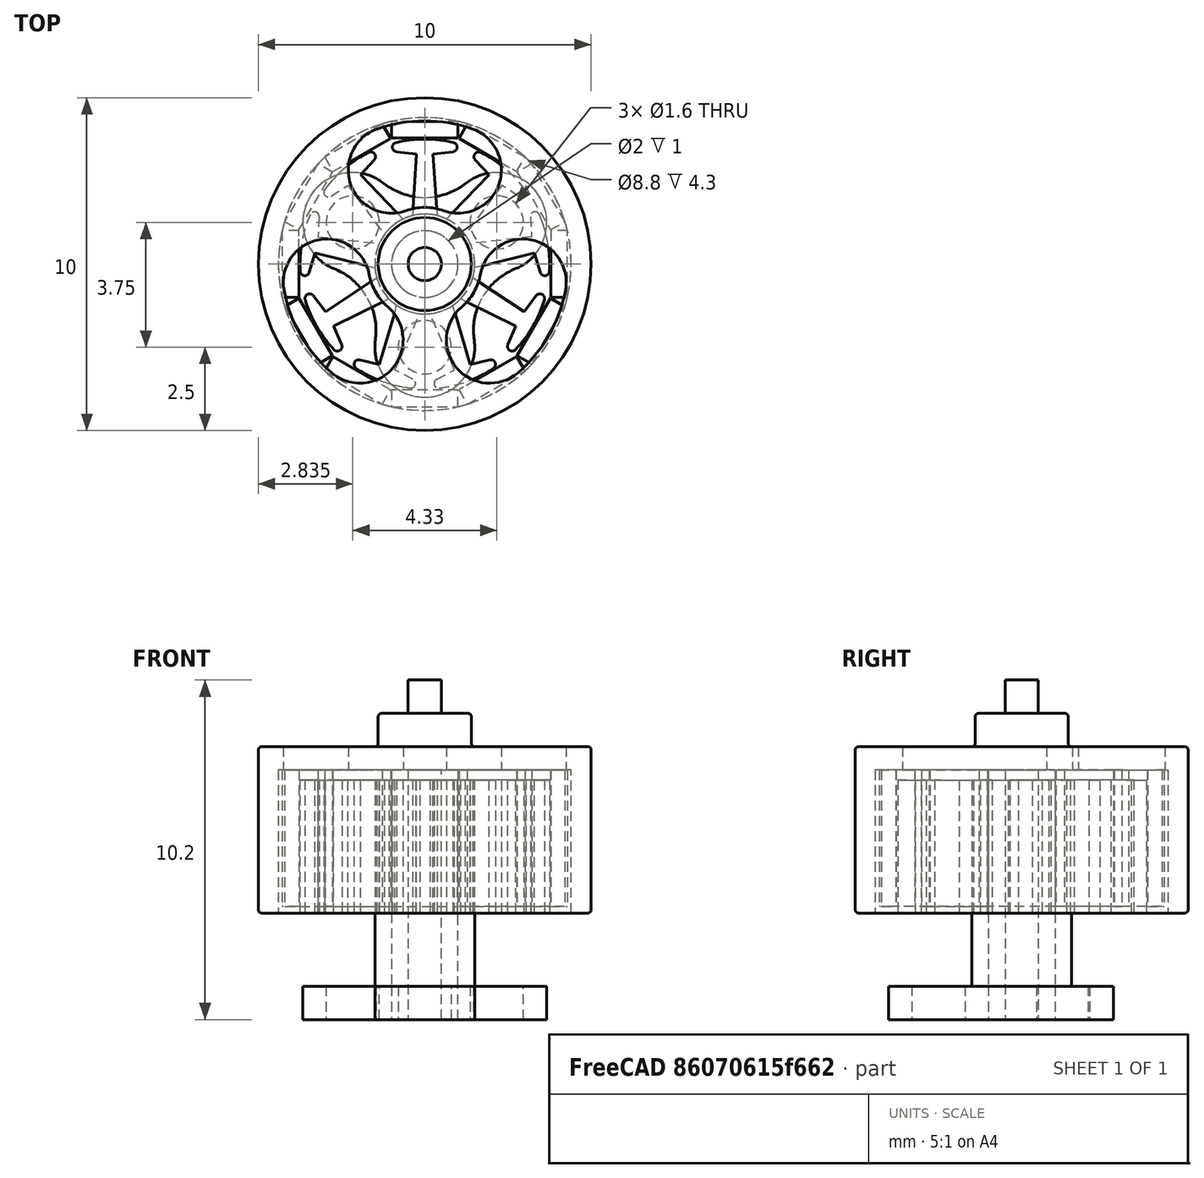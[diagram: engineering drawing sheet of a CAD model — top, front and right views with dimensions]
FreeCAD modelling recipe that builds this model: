
FCSTD DOCUMENT  (FreeCAD 0.18.1R)
Label: Moteur_D0703
License: All rights reserved
LicenseURL: http://en.wikipedia.org/wiki/All_rights_reserved
objects: Sketcher::SketchObject×9, PartDesign::Pad×7, PartDesign::PolarPattern×3, PartDesign::Pocket×2, PartDesign::Body×2, PartDesign::Fillet×1
note: 33 computed .brp shape members not serialized (recipe doc carries the construction recipe); baked Part::Feature solids carry a one-line shape summary decoded from their .brp

FEATURE [Sketcher::SketchObject] Sketch
  MapMode = 5
  Support = -> [XY_Plane]
  sketch-geometry (1):
    g0: Circle CenterX=0 CenterY=0 CenterZ=0 NormalX=0 NormalY=0 NormalZ=1 AngleXU=0 Radius=5
  constraints (2):
    c: Coincident(g0,g-1)
    c: Radius(g0) = 5
FEATURE [PartDesign::Pad] Pad
  Length = 5
  Length2 = 100
  Profile = -> Sketch
  Type = 0
FEATURE [Sketcher::SketchObject] Sketch001
  MapMode = 5
  Support = -> [XY_Plane]
  sketch-geometry (4):
    g0: ArcOfCircle CenterX=0 CenterY=0 CenterZ=0 NormalX=0 NormalY=0 NormalZ=1 AngleXU=0 Radius=1.7 StartAngle=1.23096 EndAngle=1.91064
    g1: ArcOfCircle CenterX=0 CenterY=0 CenterZ=0 NormalX=0 NormalY=0 NormalZ=1 AngleXU=0 Radius=4.3 StartAngle=1.23096 EndAngle=1.91063
    g2: ArcOfCircle CenterX=1 CenterY=2.82843 CenterZ=0 NormalX=0 NormalY=0 NormalZ=1 AngleXU=0 Radius=1.3 StartAngle=4.37256 EndAngle=7.51414
    g3: ArcOfCircle CenterX=-1 CenterY=2.82843 CenterZ=0 NormalX=0 NormalY=0 NormalZ=1 AngleXU=0 Radius=1.3 StartAngle=1.91063 EndAngle=5.05222
  constraints (12):
    c: Coincident(g0,g-1)
    c: Coincident(g1,g0)
    c: Coincident(g2,g1)
    c: Coincident(g2,g0)
    c: Coincident(g3,g0)
    c: Tangent(g3,g1) = -1.5708
    c: Tangent(g1,g2)
    c: Tangent(g2,g0)
    c: Symmetric(g2,g3,g-2)
    c: Radius(g2) = 1.3
    c: Distance(g2,g0) = 3
    c: DistanceX(g3,g2) = 2
FEATURE [PartDesign::Pocket] Pocket
  BaseFeature = -> Pad
  Length = 5
  Length2 = 100
  Profile = -> Sketch001
  Reversed = true
  Type = 1
FEATURE [PartDesign::PolarPattern] PolarPattern
  Angle = 360
  Axis = -> Sketch001 [N_Axis]
  BaseFeature = -> Pocket
  Occurrences = 3
  Originals = -> [Pocket]
FEATURE [Sketcher::SketchObject] Sketch002
  MapMode = 5
  Placement = pos=(0,0,0) rot=(1,0,0;3.14159rad)
  Support = -> [PolarPattern]
  sketch-geometry (1):
    g0: Circle CenterX=0 CenterY=0 CenterZ=0 NormalX=0 NormalY=0 NormalZ=1 AngleXU=0 Radius=4.4
  constraints (2):
    c: Coincident(g0,g-1)
    c: Radius(g0) = 4.4
FEATURE [PartDesign::Pocket] Pocket001
  BaseFeature = -> PolarPattern
  Length = 4.3
  Length2 = 100
  Profile = -> Sketch002
  Type = 0
FEATURE [Sketcher::SketchObject] Sketch003
  MapMode = 5
  Placement = pos=(0,0,5) rot=(0,0,1;0rad)
  Support = -> [Pocket001]
  sketch-geometry (1):
    g0: Circle CenterX=0 CenterY=0 CenterZ=0 NormalX=0 NormalY=0 NormalZ=1 AngleXU=0 Radius=1.4
  constraints (2):
    c: Coincident(g0,g-1)
    c: Radius(g0) = 1.4
FEATURE [PartDesign::Pad] Pad001
  BaseFeature = -> Pocket001
  Length = 1
  Length2 = 100
  Profile = -> Sketch003
  Type = 0
FEATURE [Sketcher::SketchObject] Sketch004
  MapMode = 5
  Placement = pos=(0,0,4.3) rot=(1,0,0;3.14159rad)
  Support = -> [Pad001]
  sketch-geometry (5):
    g0: LineSegment StartX=-1 StartY=4.28486 StartZ=0 EndX=1 EndY=4.28486 EndZ=0
    g1: LineSegment StartX=1 StartY=4.28486 StartZ=0 EndX=1 EndY=3.78486 EndZ=0
    g2: LineSegment StartX=1 StartY=3.78486 StartZ=0 EndX=-1 EndY=3.78486 EndZ=0
    g3: LineSegment StartX=-1 StartY=3.78486 StartZ=0 EndX=-1 EndY=4.28486 EndZ=0
    g4: Circle [constr] CenterX=0 CenterY=0 CenterZ=0 NormalX=0 NormalY=0 NormalZ=1 AngleXU=0 Radius=4.4
  constraints (13):
    c: Coincident(g0,g1)
    c: Coincident(g1,g2)
    c: Coincident(g2,g3)
    c: Coincident(g3,g0)
    c: Horizontal(g0)
    c: Vertical(g1)
    c: Vertical(g3)
    c: Symmetric(g1,g2,g-2)
    c: DistanceY(g1,g1) = 0.5
    c: Coincident(g4,g-1)
    c: Radius(g4) = 4.4
    c: PointOnObject(g0,g4)
    c: DistanceX(g0,g0) = 2
FEATURE [PartDesign::Pad] Pad002
  BaseFeature = -> Pad001
  Length = 4.1
  Length2 = 100
  Profile = -> Sketch004
  Type = 0
FEATURE [PartDesign::PolarPattern] PolarPattern001
  Angle = 360
  Axis = -> Sketch004 [N_Axis]
  BaseFeature = -> Pad002
  Occurrences = 12
  Originals = -> [Pad002]
FEATURE [Sketcher::SketchObject] Sketch005
  MapMode = 5
  Support = -> [XY_Plane001]
  sketch-geometry (10):
    g0: Circle [constr] CenterX=0 CenterY=0 CenterZ=0 NormalX=0 NormalY=0 NormalZ=1 AngleXU=0 Radius=3.75
    g1: Circle [constr] CenterX=0 CenterY=0 CenterZ=0 NormalX=0 NormalY=0 NormalZ=1 AngleXU=0 Radius=0.5
    g2: ArcOfCircle CenterX=-1e-16 CenterY=0 CenterZ=0 NormalX=0 NormalY=0 NormalZ=1 AngleXU=0 Radius=3.75 StartAngle=1.33796 EndAngle=1.80363
    g3: ArcOfCircle CenterX=0.832944 CenterY=3.51259 CenterZ=0 NormalX=0 NormalY=0 NormalZ=1 AngleXU=0 Radius=0.14 StartAngle=4.8345 EndAngle=7.62112
    g4: ArcOfCircle CenterX=-0.832948 CenterY=3.51259 CenterZ=0 NormalX=0 NormalY=0 NormalZ=1 AngleXU=0 Radius=0.14 StartAngle=1.80363 EndAngle=4.59027
    g5: LineSegment StartX=-0.850002 StartY=3.37363 StartZ=0 EndX=-0.25 EndY=3.3 EndZ=0
    g6: LineSegment StartX=0.849998 StartY=3.37363 StartZ=0 EndX=0.25 EndY=3.3 EndZ=0
    g7: LineSegment StartX=0.25 StartY=3.3 StartZ=0 EndX=0.4 EndY=0.916515 EndZ=0
    g8: LineSegment StartX=-0.25 StartY=3.3 StartZ=0 EndX=-0.4 EndY=0.916515 EndZ=0
    g9: ArcOfCircle CenterX=-1e-16 CenterY=0 CenterZ=0 NormalX=0 NormalY=0 NormalZ=1 AngleXU=0 Radius=1 StartAngle=1.15928 EndAngle=1.98231
  constraints (27):
    c: Coincident(g0,g-1)
    c: Radius(g0) = 3.75
    c: Coincident(g1,g-1)
    c: Radius(g1) = 0.5
    c: Coincident(g2,g-1)
    c: PointOnObject(g2,g0)
    c: Coincident(g3,g2)
    c: Coincident(g5,g4)
    c: Coincident(g7,g6)
    c: Coincident(g8,g5)
    c: Coincident(g9,g2)
    c: Coincident(g9,g8)
    c: Coincident(g9,g7)
    c: Radius(g9) = 1
    c: Symmetric(g8,g7,g-2)
    c: Symmetric(g6,g5,g-2)
    c: Symmetric(g2,g2,g-2)
    c: Tangent(g2,g3)
    c: Tangent(g5,g4)
    c: Radius(g3) = 0.14
    c: DistanceX(g8,g7) = 0.8
    c: DistanceX(g5,g6) = 0.5
    c: DistanceY(g2,g6) = 3.3
    c: Tangent(g4,g2) = -1.5708
    c: DistanceX(g4,g3) = 1.7
    c: Tangent(g6,g3) = 1.5708
    c: Equal(g4,g3)
FEATURE [PartDesign::Pad] Pad003
  Length = 4
  Length2 = 100
  Profile = -> Sketch005
  Type = 0
FEATURE [PartDesign::PolarPattern] PolarPattern002
  Angle = 360
  Axis = -> Sketch005 [N_Axis]
  BaseFeature = -> Pad003
  Occurrences = 9
  Originals = -> [Pad003]
FEATURE [Sketcher::SketchObject] Sketch006
  MapMode = 5
  Support = -> [XY_Plane001]
  sketch-geometry (2):
    g0: Circle CenterX=0 CenterY=0 CenterZ=0 NormalX=0 NormalY=0 NormalZ=1 AngleXU=0 Radius=1
    g1: Circle CenterX=0 CenterY=0 CenterZ=0 NormalX=0 NormalY=0 NormalZ=1 AngleXU=0 Radius=1.5
  constraints (4):
    c: Coincident(g0,g-1)
    c: Radius(g0) = 1
    c: Coincident(g1,g0)
    c: Radius(g1) = 1.5
FEATURE [PartDesign::Pad] Pad004
  BaseFeature = -> PolarPattern002
  Length = 4
  Length2 = 3.2
  Profile = -> Sketch006
  Type = 4
FEATURE [Sketcher::SketchObject] Sketch007
  MapMode = 5
  Support = -> [XY_Plane]
  sketch-geometry (1):
    g0: Circle CenterX=0 CenterY=0 CenterZ=0 NormalX=0 NormalY=0 NormalZ=1 AngleXU=0 Radius=0.5
  constraints (2):
    c: Coincident(g0,g-1)
    c: Radius(g0) = 0.5
FEATURE [PartDesign::Pad] Pad005
  BaseFeature = -> PolarPattern001
  Length = 7
  Length2 = 3.2
  Profile = -> Sketch007
  Type = 4
FEATURE [Sketcher::SketchObject] Sketch008
  MapMode = 5
  Placement = pos=(0,0,-3.2) rot=(1,0,0;3.14159rad)
  Support = -> [Pad004]
  sketch-geometry (14):
    g0: Circle [constr] CenterX=0 CenterY=0 CenterZ=0 NormalX=0 NormalY=0 NormalZ=1 AngleXU=0 Radius=2.5
    g1: Circle CenterX=0 CenterY=2.5 CenterZ=0 NormalX=0 NormalY=0 NormalZ=1 AngleXU=0 Radius=0.8
    g2: Circle CenterX=2.16506 CenterY=-1.25 CenterZ=0 NormalX=0 NormalY=0 NormalZ=1 AngleXU=0 Radius=0.8
    g3: Circle CenterX=-2.16506 CenterY=-1.25 CenterZ=0 NormalX=0 NormalY=0 NormalZ=1 AngleXU=0 Radius=0.8
    g4: LineSegment [constr] StartX=-2.16506 StartY=-1.25 StartZ=0 EndX=2.16506 EndY=-1.25 EndZ=0
    g5: LineSegment [constr] StartX=0 StartY=2.5 StartZ=0 EndX=-2.16506 EndY=-1.25 EndZ=0
    g6: ArcOfCircle CenterX=0 CenterY=2.5 CenterZ=0 NormalX=0 NormalY=0 NormalZ=1 AngleXU=0 Radius=1.5 StartAngle=6.13984 EndAngle=9.56812
    g7: ArcOfCircle CenterX=3.4641 CenterY=2 CenterZ=0 NormalX=0 NormalY=0 NormalZ=1 AngleXU=0 Radius=2 StartAngle=2.99824 EndAngle=4.33214
    g8: ArcOfCircle CenterX=2.16506 CenterY=-1.25 CenterZ=0 NormalX=0 NormalY=0 NormalZ=1 AngleXU=0 Radius=1.5 StartAngle=4.04544 EndAngle=7.47373
    g9: ArcOfCircle CenterX=0 CenterY=-4 CenterZ=0 NormalX=0 NormalY=0 NormalZ=1 AngleXU=0 Radius=2 StartAngle=0.903855 EndAngle=2.23774
    g10: ArcOfCircle CenterX=-2.16506 CenterY=-1.25 CenterZ=0 NormalX=0 NormalY=0 NormalZ=1 AngleXU=0 Radius=1.5 StartAngle=1.95105 EndAngle=5.37934
    g11: ArcOfCircle CenterX=-3.4641 CenterY=2 CenterZ=0 NormalX=0 NormalY=0 NormalZ=1 AngleXU=0 Radius=2 StartAngle=5.09264 EndAngle=6.42653
    g12: Circle [constr] CenterX=0 CenterY=0 CenterZ=0 NormalX=0 NormalY=0 NormalZ=1 AngleXU=0 Radius=2
    g13: Circle CenterX=0 CenterY=0 CenterZ=0 NormalX=0 NormalY=0 NormalZ=1 AngleXU=0 Radius=1
  constraints (40):
    c: Coincident(g0,g-1)
    c: Radius(g0) = 2.5
    c: PointOnObject(g1,g0)
    c: PointOnObject(g1,g-2)
    c: Radius(g1) = 0.8
    c: PointOnObject(g2,g0)
    c: PointOnObject(g3,g0)
    c: Equal(g3,g2)
    c: Equal(g2,g1)
    c: Horizontal(g3,g2)
    c: Coincident(g4,g3)
    c: Coincident(g4,g2)
    c: Coincident(g5,g1)
    c: Coincident(g5,g3)
    c: Equal(g5,g4)
    c: Coincident(g6,g1)
    c: Coincident(g7,g6)
    c: Coincident(g8,g2)
    c: Coincident(g8,g7)
    c: Coincident(g9,g8)
    c: Coincident(g10,g3)
    c: Coincident(g10,g9)
    c: Coincident(g11,g10)
    c: Coincident(g11,g6)
    c: Tangent(g11,g6)
    c: Tangent(g7,g6)
    c: Tangent(g7,g8)
    c: Tangent(g8,g9)
    c: Tangent(g9,g10)
    c: Coincident(g12,g-1)
    c: Radius(g12) = 2
    c: Tangent(g7,g12)
    c: Tangent(g12,g9)
    c: Tangent(g11,g12)
    c: Equal(g6,g8)
    c: Equal(g8,g10)
    c: Coincident(g13,g-1)
    c: Radius(g13) = 1
    c: Equal(g9,g11)
    c: Radius(g10) = 1.5
FEATURE [PartDesign::Pad] Pad006
  BaseFeature = -> Pad004
  Length = 1
  Length2 = 100
  Profile = -> Sketch008
  Reversed = true
  Type = 0
FEATURE [PartDesign::Body] Body001
  Group = -> [Sketch005,Pad003,PolarPattern002,Sketch006,Pad004,Sketch008,Pad006]
  Origin = -> Origin001
  Tip = -> Pad006
FEATURE [PartDesign::Fillet] Fillet
  Base = -> Pad005 [Edge3,Edge85,Edge9,Edge2]
  BaseFeature = -> Pad005
  Radius = 0.1
FEATURE [PartDesign::Body] Body
  Group = -> [Sketch,Pad,Sketch001,Pocket,PolarPattern,Sketch002,Pocket001,Sketch003,Pad001,Sketch004,Pad002,PolarPattern001,Sketch007,Pad005,Fillet]
  Origin = -> Origin
  Tip = -> Fillet
